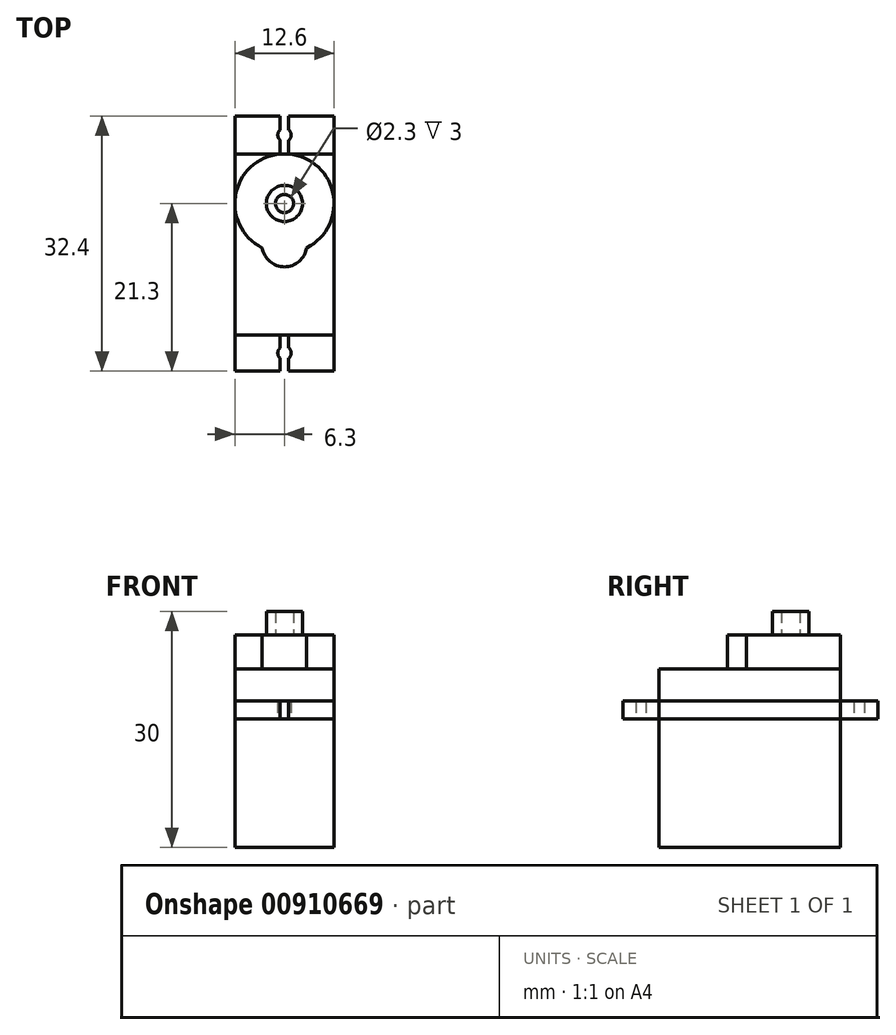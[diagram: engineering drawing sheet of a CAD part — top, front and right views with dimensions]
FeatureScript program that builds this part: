
annotation { "Feature Type Name" : "Feature", "Feature Type Description" : "" }
export const myFeature = defineFeature(function(context is Context, id is Id, definition is map)
    precondition{}
    {
        {
            var Q0;
            Q0=qCreatedBy(makeId("Top.planeOp"),FACE);
            var sketch = newSketch(context, id + "F0", { "sketchPlane" : qUnion([Q0])});
            skLineSegment(sketch, "E0.bottom", {"start": v(6.3, 11.5) * mm, "end": v(-6.3, 11.5) * mm});
            skLineSegment(sketch, "E0.top", {"start": v(6.3, -11.5) * mm, "end": v(-6.3, -11.5) * mm});
            skLineSegment(sketch, "E0.left", {"start": v(6.3, 11.5) * mm, "end": v(6.3, -11.5) * mm});
            skLineSegment(sketch, "E0.right", {"start": v(-6.3, 11.5) * mm, "end": v(-6.3, -11.5) * mm});
            skPoint(sketch, "E0.middle", {"position": v(0, 0) * mm});
            skSolve(sketch);
        }
        {
            var Q0;
            Q0=makeQuery(id+"F0.imprint","IMPRINT",FACE,{"disambiguationData":[TD([[makeQuery(id+"F0.imprint","IMPRINT",EDGE,{"derivedFrom":sQuery(id+"F0.wireOp",EDGE,"E0.bottom")}),1.0]])]});
            extrude(context, id + "F1", {"entities" : qUnion([Q0]), "depth" : 16.3 * mm, "offsetDistance" : 25 * mm});
        }
        {
            var Q0;
            Q0=makeQuery(id+"F1.opExtrude","CAP_FACE",FACE,{"disambiguationData":[OSD([sQuery(id+"F0.wireOp",EDGE,"E0.bottom"),sQuery(id+"F0.wireOp",EDGE,"E0.top"),sQuery(id+"F0.wireOp",EDGE,"E0.left"),sQuery(id+"F0.wireOp",EDGE,"E0.right")])],"isStart":false});
            var sketch = newSketch(context, id + "F2", { "sketchPlane" : qUnion([Q0])});
            skLineSegment(sketch, "E1.bottom", {"start": v(-6.3, 11.5) * mm, "end": v(6.3, 11.5) * mm});
            skLineSegment(sketch, "E1.top", {"start": v(-6.3, 16.3) * mm, "end": v(6.3, 16.3) * mm});
            skLineSegment(sketch, "E1.left", {"start": v(-6.3, 11.5) * mm, "end": v(-6.3, 16.3) * mm});
            skLineSegment(sketch, "E1.right", {"start": v(6.3, 11.5) * mm, "end": v(6.3, 16.3) * mm});
            skLineSegment(sketch, "E2.bottom", {"start": v(-6.3, -11.5) * mm, "end": v(6.3, -11.5) * mm});
            skLineSegment(sketch, "E2.top", {"start": v(-6.3, -16.1) * mm, "end": v(6.3, -16.1) * mm});
            skLineSegment(sketch, "E2.left", {"start": v(-6.3, -11.5) * mm, "end": v(-6.3, -16.1) * mm});
            skLineSegment(sketch, "E2.right", {"start": v(6.3, -11.5) * mm, "end": v(6.3, -16.1) * mm});
            skLineSegment(sketch, "E3", {"start": v(-6.3, 13.9) * mm, "end": v(0, 13.9) * mm});
            skLineSegment(sketch, "E4", {"start": v(-6.3, -13.8) * mm, "end": v(0, -13.8) * mm});
            skCircle(sketch, "E5", {"center": v(0, 13.9) * mm, "radius": 0.85 * mm});
            skCircle(sketch, "E6", {"center": v(0, -13.8) * mm, "radius": 0.85 * mm});
            skLineSegment(sketch, "E7.bottom", {"start": v(0.55, 16.3) * mm, "end": v(-0.55, 16.3) * mm});
            skLineSegment(sketch, "E7.top", {"start": v(0.55, 11.5) * mm, "end": v(-0.55, 11.5) * mm});
            skLineSegment(sketch, "E7.left", {"start": v(0.55, 16.3) * mm, "end": v(0.55, 11.5) * mm});
            skLineSegment(sketch, "E7.right", {"start": v(-0.55, 16.3) * mm, "end": v(-0.55, 11.5) * mm});
            skLineSegment(sketch, "E8.bottom", {"start": v(0.55, -11.5) * mm, "end": v(-0.55, -11.5) * mm});
            skLineSegment(sketch, "E8.top", {"start": v(0.55, -16.1) * mm, "end": v(-0.55, -16.1) * mm});
            skLineSegment(sketch, "E8.left", {"start": v(0.55, -11.5) * mm, "end": v(0.55, -16.1) * mm});
            skLineSegment(sketch, "E8.right", {"start": v(-0.55, -11.5) * mm, "end": v(-0.55, -16.1) * mm});
            skSolve(sketch);
        }
        {
            var Q0;
            {var subQ4=sQuery(id+"F2.wireOp",EDGE,"E7.top");Q0=makeQuery(id+"F2.imprint","IMPRINT",FACE,{"disambiguationData":[TD([[makeQuery(id+"F2.imprint","IMPRINT",EDGE,{"derivedFrom":subQ4}),1.0]])]});}
            var Q1;
            {var subQ1=sQuery(id+"F2.wireOp",EDGE,"E3");var subQ5=sQuery(id+"F2.wireOp",EDGE,"E1.left");var subQ6=makeQuery(id+"F2.imprint","INTERSECT",VERTEX,{"derivedFrom":[subQ5,subQ1]});Q1=makeQuery(id+"F2.imprint","IMPRINT",FACE,{"disambiguationData":[TD([[makeQuery(id+"F2.imprint","IMPRINT",EDGE,{"disambiguationData":[TD([[subQ6,-1.0]])],"derivedFrom":subQ1}),-1.0]])]});}
            var Q2;
            {var subQ5=sQuery(id+"F2.wireOp",EDGE,"E1.left");var subQ7=sQuery(id+"F2.wireOp",EDGE,"E1.top");var subQ8=makeQuery(id+"F2.imprint","INTERSECT",VERTEX,{"derivedFrom":[subQ7,subQ5]});Q2=makeQuery(id+"F2.imprint","IMPRINT",FACE,{"disambiguationData":[TD([[makeQuery(id+"F2.imprint","IMPRINT",EDGE,{"disambiguationData":[TD([[subQ8,1.0]])],"derivedFrom":subQ5}),-1.0]])]});}
            var Q3;
            {var subQ5=sQuery(id+"F2.wireOp",EDGE,"E7.top");Q3=makeQuery(id+"F2.imprint","IMPRINT",FACE,{"disambiguationData":[TD([[makeQuery(id+"F2.imprint","IMPRINT",EDGE,{"derivedFrom":subQ5}),-1.0]])]});}
            var Q4;
            {var subQ4=sQuery(id+"F2.wireOp",EDGE,"E1.right");Q4=makeQuery(id+"F2.imprint","IMPRINT",FACE,{"disambiguationData":[TD([[makeQuery(id+"F2.imprint","IMPRINT",EDGE,{"derivedFrom":subQ4}),1.0]])]});}
            var Q5;
            {var subQ0=sQuery(id+"F2.wireOp",EDGE,"E2.right");Q5=makeQuery(id+"F2.imprint","IMPRINT",FACE,{"disambiguationData":[TD([[makeQuery(id+"F2.imprint","IMPRINT",EDGE,{"derivedFrom":subQ0}),-1.0]])]});}
            var Q6;
            {var subQ5=sQuery(id+"F2.wireOp",EDGE,"E8.bottom");Q6=makeQuery(id+"F2.imprint","IMPRINT",FACE,{"disambiguationData":[TD([[makeQuery(id+"F2.imprint","IMPRINT",EDGE,{"derivedFrom":subQ5}),1.0]])]});}
            var Q7;
            {var subQ1=sQuery(id+"F2.wireOp",EDGE,"E4");var subQ5=sQuery(id+"F2.wireOp",EDGE,"E2.left");var subQ6=makeQuery(id+"F2.imprint","INTERSECT",VERTEX,{"derivedFrom":[subQ5,subQ1]});Q7=makeQuery(id+"F2.imprint","IMPRINT",FACE,{"disambiguationData":[TD([[makeQuery(id+"F2.imprint","IMPRINT",EDGE,{"disambiguationData":[TD([[subQ6,-1.0]])],"derivedFrom":subQ1}),1.0]])]});}
            var Q8;
            {var subQ5=sQuery(id+"F2.wireOp",EDGE,"E2.left");var subQ7=sQuery(id+"F2.wireOp",EDGE,"E2.top");var subQ8=makeQuery(id+"F2.imprint","INTERSECT",VERTEX,{"derivedFrom":[subQ7,subQ5]});Q8=makeQuery(id+"F2.imprint","IMPRINT",FACE,{"disambiguationData":[TD([[makeQuery(id+"F2.imprint","IMPRINT",EDGE,{"disambiguationData":[TD([[subQ8,1.0]])],"derivedFrom":subQ5}),1.0]])]});}
            extrude(context, id + "F3", {"entities" : qUnion([Q0, Q1, Q2, Q3, Q4, Q5, Q6, Q7, Q8]), "operationType" : NewBodyOperationType.ADD, "depth" : 2.3 * mm, "offsetDistance" : 25 * mm});
        }
        {
            var Q0;
            Q0=makeQuery(id+"F3.opExtrude","CAP_FACE",FACE,{"disambiguationData":[OSD([sQuery(id+"F0.wireOp",EDGE,"E0.left"),sQuery(id+"F0.wireOp",EDGE,"E0.right"),sQuery(id+"F2.wireOp",EDGE,"E1.top"),sQuery(id+"F2.wireOp",EDGE,"E1.left"),sQuery(id+"F2.wireOp",EDGE,"E1.right"),sQuery(id+"F2.wireOp",EDGE,"E2.top"),sQuery(id+"F2.wireOp",EDGE,"E2.left"),sQuery(id+"F2.wireOp",EDGE,"E2.right"),sQuery(id+"F2.wireOp",EDGE,"E5"),sQuery(id+"F2.wireOp",EDGE,"E6"),sQuery(id+"F2.wireOp",EDGE,"E7.left"),sQuery(id+"F2.wireOp",EDGE,"E7.right"),sQuery(id+"F2.wireOp",EDGE,"E8.left"),sQuery(id+"F2.wireOp",EDGE,"E8.right")])],"isStart":false});
            var sketch = newSketch(context, id + "F4", { "sketchPlane" : qUnion([Q0])});
            skLineSegment(sketch, "E9.bottom", {"start": v(6.3, 11.5) * mm, "end": v(-6.3, 11.5) * mm});
            skLineSegment(sketch, "E9.top", {"start": v(6.3, -11.5) * mm, "end": v(-6.3, -11.5) * mm});
            skLineSegment(sketch, "E9.left", {"start": v(6.3, 11.5) * mm, "end": v(6.3, -11.5) * mm});
            skLineSegment(sketch, "E9.right", {"start": v(-6.3, 11.5) * mm, "end": v(-6.3, -11.5) * mm});
            skPoint(sketch, "E9.middle", {"position": v(0, 0) * mm});
            skSolve(sketch);
        }
        {
            var Q0;
            Q0=makeQuery(id+"F4.imprint","IMPRINT",FACE,{"disambiguationData":[TD([[makeQuery(id+"F4.imprint","IMPRINT",EDGE,{"derivedFrom":sQuery(id+"F4.wireOp",EDGE,"E9.bottom")}),1.0]])]});
            extrude(context, id + "F5", {"entities" : qUnion([Q0]), "operationType" : NewBodyOperationType.ADD, "depth" : 4.1 * mm, "offsetDistance" : 25 * mm});
        }
        {
            var Q0;
            Q0=makeQuery(id+"F5.opExtrude","CAP_FACE",FACE,{"disambiguationData":[OSD([sQuery(id+"F4.wireOp",EDGE,"E9.bottom"),sQuery(id+"F4.wireOp",EDGE,"E9.top"),sQuery(id+"F4.wireOp",EDGE,"E9.left"),sQuery(id+"F4.wireOp",EDGE,"E9.right")])],"isStart":false});
            var sketch = newSketch(context, id + "F6", { "sketchPlane" : qUnion([Q0])});
            skLineSegment(sketch, "E10", {"start": v(0, 11.5) * mm, "end": v(0, 5.2) * mm});
            skCircle(sketch, "E11", {"center": v(0, 5.2) * mm, "radius": 6.3 * mm});
            skLineSegment(sketch, "E12", {"start": v(0, 11.5) * mm, "end": v(0, -0.25) * mm});
            skCircle(sketch, "E13", {"center": v(0, 0) * mm, "radius": 2.85 * mm});
            skSolve(sketch);
        }
        {
            var Q0;
            {var subQ0=sQuery(id+"F6.wireOp",EDGE,"E12");var subQ1=makeQuery(id+"F6.imprint","IMPRINT",VERTEX,{"derivedFrom":subQ0});Q0=makeQuery(id+"F6.imprint","IMPRINT",FACE,{"disambiguationData":[TD([[makeQuery(id+"F6.imprint","IMPRINT",EDGE,{"disambiguationData":[TD([[subQ1,-1.0]])],"derivedFrom":subQ0}),1.0]])]});}
            var Q1;
            {var subQ0=sQuery(id+"F6.wireOp",EDGE,"E12");var subQ3=makeQuery(id+"F6.imprint","IMPRINT",VERTEX,{"derivedFrom":subQ0});Q1=makeQuery(id+"F6.imprint","IMPRINT",FACE,{"disambiguationData":[TD([[makeQuery(id+"F6.imprint","IMPRINT",EDGE,{"disambiguationData":[TD([[subQ3,-1.0]])],"derivedFrom":subQ0}),-1.0]])]});}
            var Q2;
            {var subQ0=sQuery(id+"F6.wireOp",EDGE,"E13");var subQ1=sQuery(id+"F6.wireOp",EDGE,"E11");var subQ2=makeQuery(id+"F6.imprint","INTERSECT",VERTEX,{"disambiguationData":[OD(0.0)],"derivedFrom":[subQ1,subQ0]});Q2=makeQuery(id+"F6.imprint","IMPRINT",FACE,{"disambiguationData":[TD([[makeQuery(id+"F6.imprint","IMPRINT",EDGE,{"disambiguationData":[TD([[subQ2,-1.0]])],"derivedFrom":subQ1}),1.0]])]});}
            var Q3;
            {var subQ0=sQuery(id+"F6.wireOp",EDGE,"E13");var subQ1=sQuery(id+"F6.wireOp",EDGE,"E11");var subQ2=makeQuery(id+"F6.imprint","INTERSECT",VERTEX,{"disambiguationData":[OD(0.0)],"derivedFrom":[subQ1,subQ0]});Q3=makeQuery(id+"F6.imprint","IMPRINT",FACE,{"disambiguationData":[TD([[makeQuery(id+"F6.imprint","IMPRINT",EDGE,{"disambiguationData":[TD([[subQ2,-1.0]])],"derivedFrom":subQ1}),-1.0]])]});}
            extrude(context, id + "F7", {"entities" : qUnion([Q0, Q1, Q2, Q3]), "operationType" : NewBodyOperationType.ADD, "depth" : 4.3 * mm, "offsetDistance" : 25 * mm});
        }
        {
            var Q0;
            Q0=makeQuery(id+"F7.opExtrude","CAP_FACE",FACE,{"disambiguationData":[OSD([sQuery(id+"F6.wireOp",EDGE,"E11"),sQuery(id+"F6.wireOp",EDGE,"E13")])],"isStart":false});
            var sketch = newSketch(context, id + "F8", { "sketchPlane" : qUnion([Q0])});
            skCircle(sketch, "E14", {"center": v(0, 5.2) * mm, "radius": 2.3 * mm});
            skCircle(sketch, "E15", {"center": v(0, 5.2) * mm, "radius": 1.15 * mm});
            skSolve(sketch);
        }
        {
            var Q0;
            Q0=makeQuery(id+"F8.imprint","IMPRINT",FACE,{"disambiguationData":[TD([[makeQuery(id+"F8.imprint","IMPRINT",EDGE,{"derivedFrom":sQuery(id+"F8.wireOp",EDGE,"E14")}),1.0]])]});
            extrude(context, id + "F9", {"entities" : qUnion([Q0]), "operationType" : NewBodyOperationType.ADD, "depth" : 3 * mm, "offsetDistance" : 25 * mm});
        }
    });
